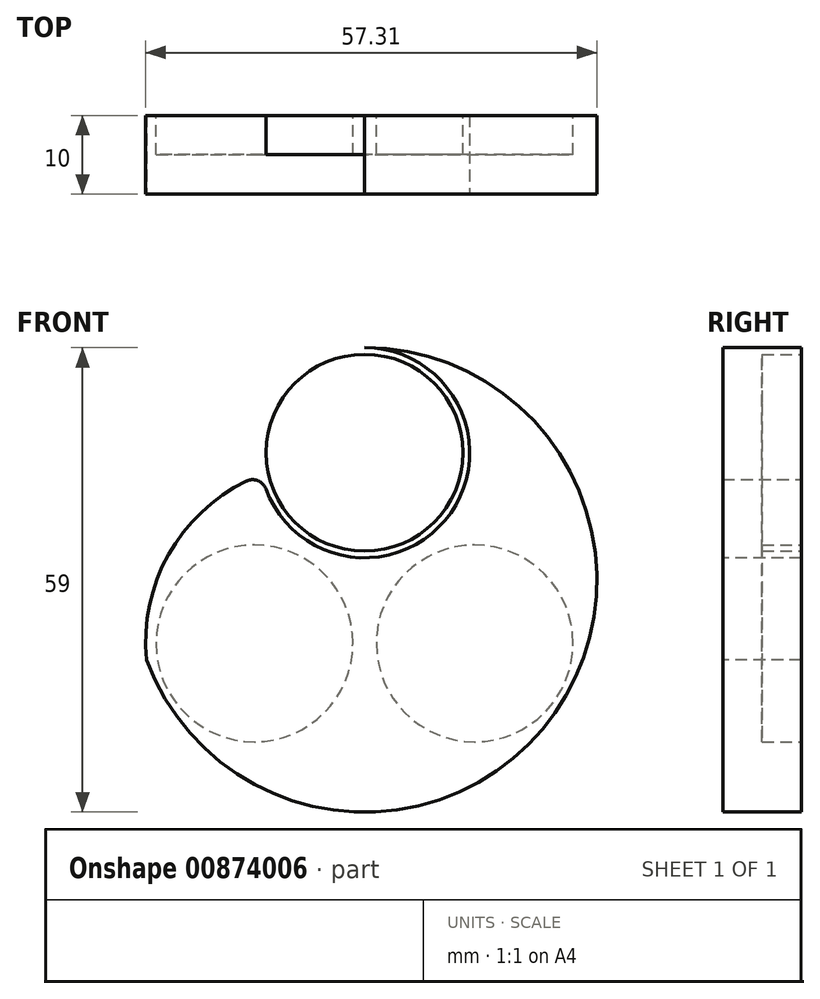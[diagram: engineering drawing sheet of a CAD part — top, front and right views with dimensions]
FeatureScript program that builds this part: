
annotation { "Feature Type Name" : "Feature", "Feature Type Description" : "" }
export const myFeature = defineFeature(function(context is Context, id is Id, definition is map)
    precondition{}
    {
        {
            var Q0;
            Q0=qCreatedBy(makeId("Front.planeOp"),FACE);
            var sketch = newSketch(context, id + "F0", { "sketchPlane" : qUnion([Q0])});
            skCircle(sketch, "E0", {"center": v(0, 0) * mm, "radius": 29.5 * mm});
            skSolve(sketch);
        }
        {
            var Q0;
            Q0 = qSketchRegion(id + "F0", true);
            extrude(context, id + "F1", {"entities" : qUnion([Q0]), "depth" : 10 * mm, "offsetDistance" : 25 * mm});
        }
        {
            var Q0;
            Q0=makeQuery(id+"F1.opExtrude","CAP_FACE",FACE,{"disambiguationData":[OSD([sQuery(id+"F0.wireOp",EDGE,"E0")])],"isStart":false});
            var sketch = newSketch(context, id + "F2", { "sketchPlane" : qUnion([Q0])});
            skCircle(sketch, "E1", {"center": v(0, 16.15) * mm, "radius": 13.35 * mm});
            skArc(sketch, "E2", {"start": v(-13.06, 13.39) * mm, "mid": v(-24.38, 4.1) * mm, "end": v(-27.7, -10.14) * mm});
            skSolve(sketch);
        }
        {
            var Q0;
            {var subQ0=sQuery(id+"F2.wireOp",EDGE,"E1");var subQ1=makeQuery(id+"F2.imprint","INTERSECT",VERTEX,{"derivedFrom":[subQ0,sQuery(id+"F2.wireOp",EDGE,"E2")]});Q0=makeQuery(id+"F2.imprint","IMPRINT",FACE,{"disambiguationData":[TD([[makeQuery(id+"F2.imprint","IMPRINT",EDGE,{"disambiguationData":[TD([[subQ1,1.0]])],"derivedFrom":subQ0}),1.0]])]});}
            var Q1;
            {var subQ0=sQuery(id+"F2.wireOp",EDGE,"E2");Q1=makeQuery(id+"F2.imprint","IMPRINT",FACE,{"disambiguationData":[TD([[makeQuery(id+"F2.imprint","IMPRINT",EDGE,{"derivedFrom":subQ0}),-1.0]])]});}
            extrude(context, id + "F3", {"entities" : qUnion([Q0, Q1]), "operationType" : NewBodyOperationType.REMOVE, "endBound" : BoundingType.THROUGH_ALL, "oppositeDirection" : true, "depth" : 25 * mm, "offsetDistance" : 25 * mm});
        }
        {
            var Q0;
            Q0=makeQuery(id+"F7sk6ZShS9oHfl1_1.1.F3.boolean.opBoolean","COPY",EDGE,{"derivedFrom":makeQuery(id+"F7sk6ZShS9oHfl1_1.1.F3.opExtrude","SWEPT_EDGE",EDGE,{"disambiguationData":[OSD([sQuery(id+"F2.wireOp",EDGE,"E1"),sQuery(id+"F2.wireOp",EDGE,"E2")])]})});
            var Q1;
            Q1=makeQuery(id+"F7sk6ZShS9oHfl1_1.2.F3.boolean.opBoolean","COPY",EDGE,{"derivedFrom":makeQuery(id+"F7sk6ZShS9oHfl1_1.2.F3.opExtrude","SWEPT_EDGE",EDGE,{"disambiguationData":[OSD([sQuery(id+"F2.wireOp",EDGE,"E1"),sQuery(id+"F2.wireOp",EDGE,"E2")])]})});
            var Q2;
            Q2=makeQuery(id+"F3.boolean.opBoolean","COPY",EDGE,{"derivedFrom":makeQuery(id+"F3.opExtrude","SWEPT_EDGE",EDGE,{"disambiguationData":[OSD([sQuery(id+"F2.wireOp",EDGE,"E1"),sQuery(id+"F2.wireOp",EDGE,"E2")])]})});
            fillet(context, id + "F4", {"entities" : qUnion([Q0, Q1, Q2]), "radius" : 1.8 * mm, "tangentPropagation" : true, "allowEdgeOverflow" : false});
        }
        {
            var Q0;
            Q0=qCreatedBy(makeId("Front.planeOp"),FACE);
            var sketch = newSketch(context, id + "F5", { "sketchPlane" : qUnion([Q0])});
            skCircle(sketch, "E3", {"center": v(-13.99, -8.07) * mm, "radius": 12.5 * mm});
            skSolve(sketch);
        }
        {
            var Q0;
            Q0=makeQuery(id+"F5.imprint","IMPRINT",FACE,{"disambiguationData":[TD([[makeQuery(id+"F5.imprint","IMPRINT",EDGE,{"derivedFrom":sQuery(id+"F5.wireOp",EDGE,"E3")}),1.0]])]});
            extrude(context, id + "F6", {"entities" : qUnion([Q0]), "depth" : 5 * mm, "offsetDistance" : 25 * mm});
        }
        {
            var Q0;
            Q0=makeQuery(id+"F6.opExtrude","SWEPT_BODY",BODY,{"disambiguationData":[OSD([sQuery(id+"F5.wireOp",EDGE,"E3")])]});
            var Q1;
            {var subQ0=sQuery(id+"F0.wireOp",EDGE,"E0");var subQ2=makeQuery(id+"F7sk6ZShS9oHfl1_1.1.F3.opExtrude","SWEPT_FACE",FACE,{"disambiguationData":[OSD([sQuery(id+"F2.wireOp",EDGE,"E1")])]});var subQ4=sQuery(id+"F2.wireOp",EDGE,"E2");Q1=makeQuery(id+"F7sk6ZShS9oHfl1_1.2.F3.boolean.opBoolean","SPLIT",FACE,{"disambiguationData":[TD([makeQuery(id+"F7sk6ZShS9oHfl1_1.1.F3.boolean.opBoolean","COPY",FACE,{"derivedFrom":subQ2})])],"derivedFrom":makeQuery(id+"F7sk6ZShS9oHfl1_1.1.F3.boolean.opBoolean","SPLIT",FACE,{"disambiguationData":[TD([makeQuery(id+"F3.boolean.opBoolean","COPY",FACE,{"derivedFrom":makeQuery(id+"F3.opExtrude","SWEPT_FACE",FACE,{"disambiguationData":[OSD([subQ4])]})})])],"derivedFrom":makeQuery(id+"F1.opExtrude","SWEPT_FACE",FACE,{"disambiguationData":[OSD([subQ0])]})})});}
            circularPattern(context, id + "F7", {"entities" : qUnion([Q0]), "axis" : qUnion([Q1]), "angle" : 360 * degree, "instanceCount" : 3, "equalSpace" : true});
        }
    });
